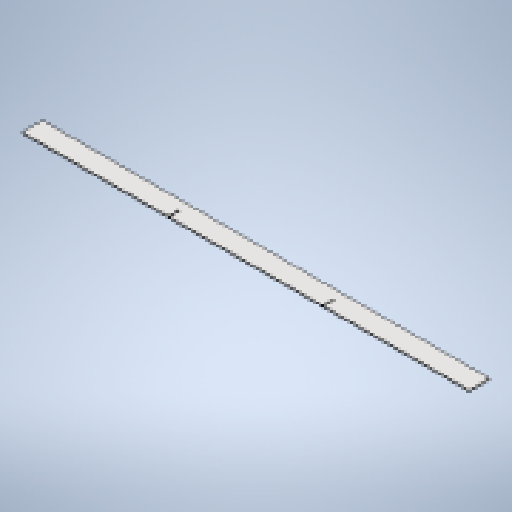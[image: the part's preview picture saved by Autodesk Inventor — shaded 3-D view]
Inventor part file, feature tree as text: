
AUTODESK INVENTOR PART (.ipt)
format: ipt  version: 2025 (Build 290162010, 162A)  size: 195,584 bytes
history: native  units: mm
features: sketch x3, extrude x2, sheet_metal_op x1, other x1, projected_geometry x1
ambient origin geometry x8: Origin, YZ Plane, XZ Plane, XY Plane, X Axis, Y Axis, Z Axis, Center Point
bodies: Body1 (feature_tree)
feature tree (8):
  sheet_metal_op  "Face1"
  extrude  "Extrusion1"  Depth=50.0mm
  extrude  "Extrusion2"  Depth=50.0mm
  sketch  "Sketch1"  dims[d16=50.0mm d17=1200.0mm]
  other  "Plate2"
  sketch  "Sketch2"  dims[d18=50.0mm d19=50.0mm]
  sketch  "Sketch3"  dims[d20=3.0mm d21=190.0mm d22=3.0mm d23=26.0mm d24=0.0mm d25=0.0mm d29=190.0mm d30=3.0mm d31=26.0mm d32=2.0mm d33=8.726646mm d34=50.0mm d35=50.0mm d36=0.0mm d37=0.0mm]
  projected_geometry  "Projected Loop1"
